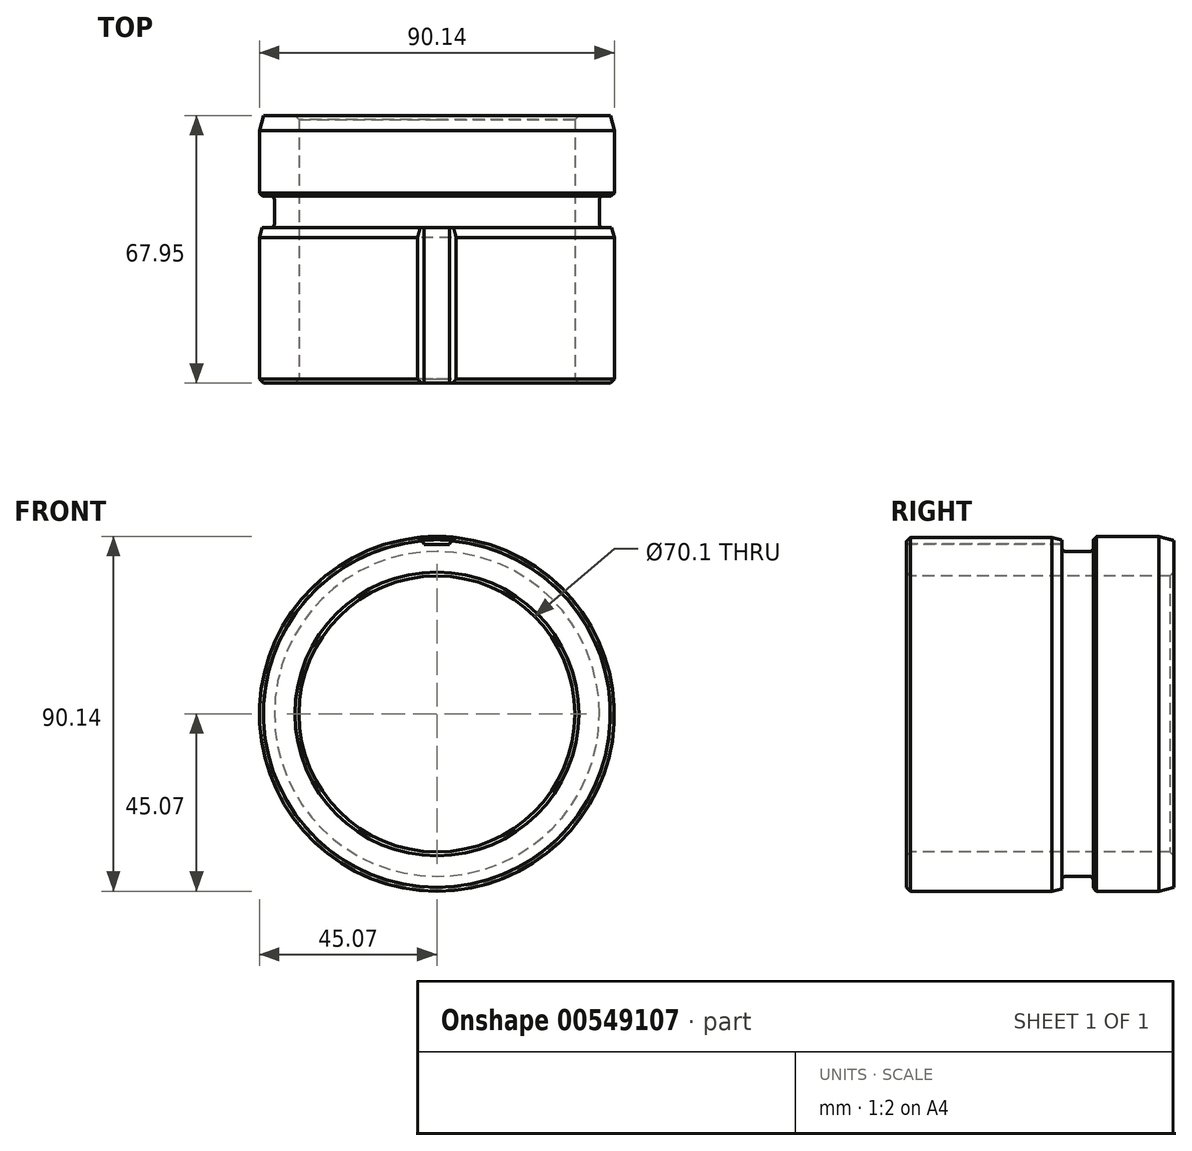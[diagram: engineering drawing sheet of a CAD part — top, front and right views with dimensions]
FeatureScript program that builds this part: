
annotation { "Feature Type Name" : "Feature", "Feature Type Description" : "" }
export const myFeature = defineFeature(function(context is Context, id is Id, definition is map)
    precondition{}
    {
        {
            var Q0;
            Q0=qCreatedBy(makeId("Right.planeOp"),FACE);
            var sketch = newSketch(context, id + "F0", { "sketchPlane" : qUnion([Q0])});
            skLineSegment(sketch, "E0.bottom", {"start": v(0, 45.07) * mm, "end": v(67.95, 45.07) * mm});
            skLineSegment(sketch, "E0.top", {"start": v(0, 35.05) * mm, "end": v(67.95, 35.05) * mm});
            skLineSegment(sketch, "E0.left", {"start": v(0, 45.07) * mm, "end": v(0, 35.05) * mm});
            skLineSegment(sketch, "E0.right", {"start": v(67.95, 45.07) * mm, "end": v(67.95, 35.05) * mm});
            skLineSegment(sketch, "E1", {"start": v(0, 0) * mm, "end": v(20.14, 0) * mm, "construction": true});
            skSolve(sketch);
        }
        {
            var Q0;
            Q0=makeQuery(id+"F0.imprint","IMPRINT",FACE,{"disambiguationData":[TD([[makeQuery(id+"F0.imprint","IMPRINT",EDGE,{"derivedFrom":sQuery(id+"F0.wireOp",EDGE,"E0.bottom")}),-1.0]])]});
            var Q1;
            Q1=sQuery(id+"F0.wireOp",EDGE,"E1");
            revolve(context, id + "F1", {"entities" : qUnion([Q0]), "axis" : qUnion([Q1]), "revolveType" : RevolveType.FULL});
        }
        {
            var Q0;
            Q0=makeQuery(id+"F1.opRevolve","SWEPT_EDGE",EDGE,{"disambiguationData":[OSD([sQuery(id+"F0.wireOp",EDGE,"E0.top"),sQuery(id+"F0.wireOp",EDGE,"E0.left")])]});
            var Q1;
            Q1=makeQuery(id+"F1.opRevolve","SWEPT_EDGE",EDGE,{"disambiguationData":[OSD([sQuery(id+"F0.wireOp",EDGE,"E0.bottom"),sQuery(id+"F0.wireOp",EDGE,"E0.left")])]});
            var Q2;
            Q2=makeQuery(id+"F1.opRevolve","SWEPT_EDGE",EDGE,{"disambiguationData":[OSD([sQuery(id+"F0.wireOp",EDGE,"E0.top"),sQuery(id+"F0.wireOp",EDGE,"E0.right")])]});
            chamfer(context, id + "F2", {"entities" : qUnion([Q0, Q1, Q2]), "width" : 1 * mm, "tangentPropagation" : true});
        }
        {
            var Q0;
            Q0=makeQuery(id+"F1.opRevolve","SWEPT_EDGE",EDGE,{"disambiguationData":[OSD([sQuery(id+"F0.wireOp",EDGE,"E0.bottom"),sQuery(id+"F0.wireOp",EDGE,"E0.right")])]});
            chamfer(context, id + "F3", {"entities" : qUnion([Q0]), "chamferType" : ChamferType.OFFSET_ANGLE, "width" : 3.8 * mm, "oppositeDirection" : false, "angle" : 15 * degree, "tangentPropagation" : true});
        }
        {
            var Q0;
            Q0=qCreatedBy(makeId("Right.planeOp"),FACE);
            var sketch = newSketch(context, id + "F4", { "sketchPlane" : qUnion([Q0])});
            skLineSegment(sketch, "E2.bottom", {"start": v(39.5, 51.13) * mm, "end": v(47.5, 51.13) * mm});
            skLineSegment(sketch, "E2.top", {"start": v(39.5, 41.28) * mm, "end": v(47.5, 41.28) * mm});
            skLineSegment(sketch, "E2.left", {"start": v(39.5, 51.13) * mm, "end": v(39.5, 41.28) * mm});
            skLineSegment(sketch, "E2.right", {"start": v(47.5, 51.13) * mm, "end": v(47.5, 41.28) * mm});
            skLineSegment(sketch, "E3", {"start": v(0, 0) * mm, "end": v(67, 0) * mm, "construction": true});
            skSolve(sketch);
        }
        {
            var Q0;
            Q0 = qSketchRegion(id + "F4", true);
            var Q1;
            Q1=sQuery(id+"F4.wireOp",EDGE,"E3");
            revolve(context, id + "F5", {"operationType" : NewBodyOperationType.REMOVE, "entities" : qUnion([Q0]), "axis" : qUnion([Q1]), "revolveType" : RevolveType.FULL});
        }
        {
            var Q0;
            Q0=makeQuery(id+"F1.opRevolve","SWEPT_FACE",FACE,{"disambiguationData":[OSD([sQuery(id+"F0.wireOp",EDGE,"E0.left")])]});
            var sketch = newSketch(context, id + "F6", { "sketchPlane" : qUnion([Q0])});
            skLineSegment(sketch, "E4.bottom", {"start": v(0, 49.68) * mm, "end": v(3.25, 49.68) * mm});
            skLineSegment(sketch, "E4.top", {"start": v(0, 43.07) * mm, "end": v(3.25, 43.07) * mm});
            skLineSegment(sketch, "E4.left", {"start": v(0, 49.68) * mm, "end": v(0, 43.07) * mm, "construction": true});
            skLineSegment(sketch, "E4.right", {"start": v(3.25, 49.68) * mm, "end": v(3.25, 43.07) * mm});
            skLineSegment(sketch, "E5.MirrorCS", {"start": v(0, 49.68) * mm, "end": v(-3.25, 49.68) * mm});
            skLineSegment(sketch, "E6.MirrorCS", {"start": v(-3.25, 49.68) * mm, "end": v(-3.25, 43.07) * mm});
            skLineSegment(sketch, "E7.MirrorCS", {"start": v(0, 43.07) * mm, "end": v(-3.25, 43.07) * mm});
            skSolve(sketch);
        }
        {
            var Q0;
            Q0 = qSketchRegion(id + "F6", true);
            extrude(context, id + "F7", {"entities" : qUnion([Q0]), "operationType" : NewBodyOperationType.REMOVE, "oppositeDirection" : true, "depth" : 40 * mm, "offsetDistance" : 25.4 * mm});
        }
        {
            var Q0;
            {var subQ0=sQuery(id+"F0.wireOp",EDGE,"E0.bottom");Q0=makeQuery(id+"F7.boolean.opBoolean","INTERSECT",EDGE,{"derivedFrom":[makeQuery(id+"F5.boolean.opBoolean","SPLIT",FACE,{"disambiguationData":[TD([makeQuery(id+"F5.opRevolve","SWEPT_FACE",FACE,{"disambiguationData":[OSD([sQuery(id+"F4.wireOp",EDGE,"E2.left")])]})])],"derivedFrom":makeQuery(id+"F1.opRevolve","SWEPT_FACE",FACE,{"disambiguationData":[OSD([subQ0])]})}),makeQuery(id+"F7.opExtrude","SWEPT_FACE",FACE,{"disambiguationData":[OSD([sQuery(id+"F6.wireOp",EDGE,"E6.MirrorCS")])]})]});}
            var Q1;
            {var subQ0=sQuery(id+"F0.wireOp",EDGE,"E0.bottom");Q1=makeQuery(id+"F7.boolean.opBoolean","INTERSECT",EDGE,{"derivedFrom":[makeQuery(id+"F5.boolean.opBoolean","SPLIT",FACE,{"disambiguationData":[TD([makeQuery(id+"F5.opRevolve","SWEPT_FACE",FACE,{"disambiguationData":[OSD([sQuery(id+"F4.wireOp",EDGE,"E2.left")])]})])],"derivedFrom":makeQuery(id+"F1.opRevolve","SWEPT_FACE",FACE,{"disambiguationData":[OSD([subQ0])]})}),makeQuery(id+"F7.opExtrude","SWEPT_FACE",FACE,{"disambiguationData":[OSD([sQuery(id+"F6.wireOp",EDGE,"E4.right")])]})]});}
            chamfer(context, id + "F8", {"entities" : qUnion([Q0, Q1]), "width" : 1.5 * mm, "tangentPropagation" : true});
        }
        {
            var Q0;
            Q0=makeQuery(id+"F5.boolean.opBoolean","COPY",EDGE,{"derivedFrom":makeQuery(id+"F5.opRevolve","SWEPT_EDGE",EDGE,{"disambiguationData":[OSD([sQuery(id+"F4.wireOp",EDGE,"E2.top"),sQuery(id+"F4.wireOp",EDGE,"E2.left")])]})});
            var Q1;
            Q1=makeQuery(id+"F5.boolean.opBoolean","COPY",EDGE,{"derivedFrom":makeQuery(id+"F5.opRevolve","SWEPT_EDGE",EDGE,{"disambiguationData":[OSD([sQuery(id+"F4.wireOp",EDGE,"E2.top"),sQuery(id+"F4.wireOp",EDGE,"E2.right")])]})});
            fillet(context, id + "F9", {"entities" : qUnion([Q0, Q1]), "radius" : 1 * mm, "tangentPropagation" : true, "allowEdgeOverflow" : false});
        }
        {
            var Q0;
            Q0=makeQuery(id+"F5.boolean.opBoolean","INTERSECT",EDGE,{"derivedFrom":[makeQuery(id+"F1.opRevolve","SWEPT_FACE",FACE,{"disambiguationData":[OSD([sQuery(id+"F0.wireOp",EDGE,"E0.bottom")])]}),makeQuery(id+"F5.opRevolve","SWEPT_FACE",FACE,{"disambiguationData":[OSD([sQuery(id+"F4.wireOp",EDGE,"E2.right")])]})]});
            chamfer(context, id + "F10", {"entities" : qUnion([Q0]), "width" : 0.81 * mm, "tangentPropagation" : true});
        }
        {
            var Q0;
            {var subQ0=sQuery(id+"F0.wireOp",EDGE,"E0.bottom");var subQ1=makeQuery(id+"F1.opRevolve","SWEPT_FACE",FACE,{"disambiguationData":[OSD([subQ0])]});var subQ2=makeQuery(id+"F5.opRevolve","SWEPT_FACE",FACE,{"disambiguationData":[OSD([sQuery(id+"F4.wireOp",EDGE,"E2.left")])]});var subQ5=sQuery(id+"F6.wireOp",EDGE,"E6.MirrorCS");Q0=makeQuery(id+"F7MiCg9jpVJxh7S_1.3.F7.boolean.opBoolean","SPLIT",EDGE,{"disambiguationData":[TD([makeQuery(id+"F7MiCg9jpVJxh7S_1.3.F7.opExtrude","SWEPT_FACE",FACE,{"disambiguationData":[OSD([subQ5])]})])],"derivedFrom":makeQuery(id+"F7MiCg9jpVJxh7S_1.2.F7.boolean.opBoolean","SPLIT",EDGE,{"disambiguationData":[TD([makeQuery(id+"F7MiCg9jpVJxh7S_1.2.F7.opExtrude","SWEPT_FACE",FACE,{"disambiguationData":[OSD([subQ5])]})])],"derivedFrom":makeQuery(id+"F7MiCg9jpVJxh7S_1.1.F7.boolean.opBoolean","SPLIT",EDGE,{"disambiguationData":[TD([makeQuery(id+"F7MiCg9jpVJxh7S_1.1.F7.opExtrude","SWEPT_FACE",FACE,{"disambiguationData":[OSD([subQ5])]})])],"derivedFrom":makeQuery(id+"F5.boolean.opBoolean","INTERSECT",EDGE,{"derivedFrom":[subQ1,subQ2]})})})});}
            var Q1;
            {var subQ0=sQuery(id+"F0.wireOp",EDGE,"E0.bottom");var subQ1=makeQuery(id+"F1.opRevolve","SWEPT_FACE",FACE,{"disambiguationData":[OSD([subQ0])]});var subQ2=makeQuery(id+"F5.opRevolve","SWEPT_FACE",FACE,{"disambiguationData":[OSD([sQuery(id+"F4.wireOp",EDGE,"E2.left")])]});Q1=makeQuery(id+"F7MiCg9jpVJxh7S_1.1.F7.boolean.opBoolean","SPLIT",EDGE,{"disambiguationData":[TD([makeQuery(id+"F7MiCg9jpVJxh7S_1.1.F7.opExtrude","SWEPT_FACE",FACE,{"disambiguationData":[OSD([sQuery(id+"F6.wireOp",EDGE,"E4.right")])]})])],"derivedFrom":makeQuery(id+"F5.boolean.opBoolean","INTERSECT",EDGE,{"derivedFrom":[subQ1,subQ2]})});}
            var Q2;
            {var subQ0=sQuery(id+"F0.wireOp",EDGE,"E0.bottom");var subQ1=makeQuery(id+"F1.opRevolve","SWEPT_FACE",FACE,{"disambiguationData":[OSD([subQ0])]});var subQ2=makeQuery(id+"F5.opRevolve","SWEPT_FACE",FACE,{"disambiguationData":[OSD([sQuery(id+"F4.wireOp",EDGE,"E2.left")])]});var subQ4=sQuery(id+"F6.wireOp",EDGE,"E4.right");var subQ5=sQuery(id+"F6.wireOp",EDGE,"E6.MirrorCS");Q2=makeQuery(id+"F7MiCg9jpVJxh7S_1.3.F7.boolean.opBoolean","SPLIT",EDGE,{"disambiguationData":[TD([makeQuery(id+"F7MiCg9jpVJxh7S_1.3.F7.opExtrude","SWEPT_FACE",FACE,{"disambiguationData":[OSD([subQ4])]})])],"derivedFrom":makeQuery(id+"F7MiCg9jpVJxh7S_1.2.F7.boolean.opBoolean","SPLIT",EDGE,{"disambiguationData":[TD([makeQuery(id+"F7MiCg9jpVJxh7S_1.2.F7.opExtrude","SWEPT_FACE",FACE,{"disambiguationData":[OSD([subQ5])]})])],"derivedFrom":makeQuery(id+"F7MiCg9jpVJxh7S_1.1.F7.boolean.opBoolean","SPLIT",EDGE,{"disambiguationData":[TD([makeQuery(id+"F7MiCg9jpVJxh7S_1.1.F7.opExtrude","SWEPT_FACE",FACE,{"disambiguationData":[OSD([subQ5])]})])],"derivedFrom":makeQuery(id+"F5.boolean.opBoolean","INTERSECT",EDGE,{"derivedFrom":[subQ1,subQ2]})})})});}
            var Q3;
            {var subQ0=sQuery(id+"F0.wireOp",EDGE,"E0.bottom");var subQ1=makeQuery(id+"F1.opRevolve","SWEPT_FACE",FACE,{"disambiguationData":[OSD([subQ0])]});var subQ2=sQuery(id+"F6.wireOp",EDGE,"E6.MirrorCS");var subQ3=makeQuery(id+"F5.opRevolve","SWEPT_FACE",FACE,{"disambiguationData":[OSD([sQuery(id+"F4.wireOp",EDGE,"E2.left")])]});var subQ5=sQuery(id+"F6.wireOp",EDGE,"E4.right");Q3=makeQuery(id+"F7MiCg9jpVJxh7S_1.2.F7.boolean.opBoolean","SPLIT",EDGE,{"disambiguationData":[TD([makeQuery(id+"F7MiCg9jpVJxh7S_1.2.F7.opExtrude","SWEPT_FACE",FACE,{"disambiguationData":[OSD([subQ5])]})])],"derivedFrom":makeQuery(id+"F7MiCg9jpVJxh7S_1.1.F7.boolean.opBoolean","SPLIT",EDGE,{"disambiguationData":[TD([makeQuery(id+"F7MiCg9jpVJxh7S_1.1.F7.opExtrude","SWEPT_FACE",FACE,{"disambiguationData":[OSD([subQ2])]})])],"derivedFrom":makeQuery(id+"F5.boolean.opBoolean","INTERSECT",EDGE,{"derivedFrom":[subQ1,subQ3]})})});}
            chamfer(context, id + "F11", {"entities" : qUnion([Q0, Q1, Q2, Q3]), "chamferType" : ChamferType.OFFSET_ANGLE, "width" : 2.54 * mm, "oppositeDirection" : false, "angle" : 15 * degree, "tangentPropagation" : true});
        }
    });
